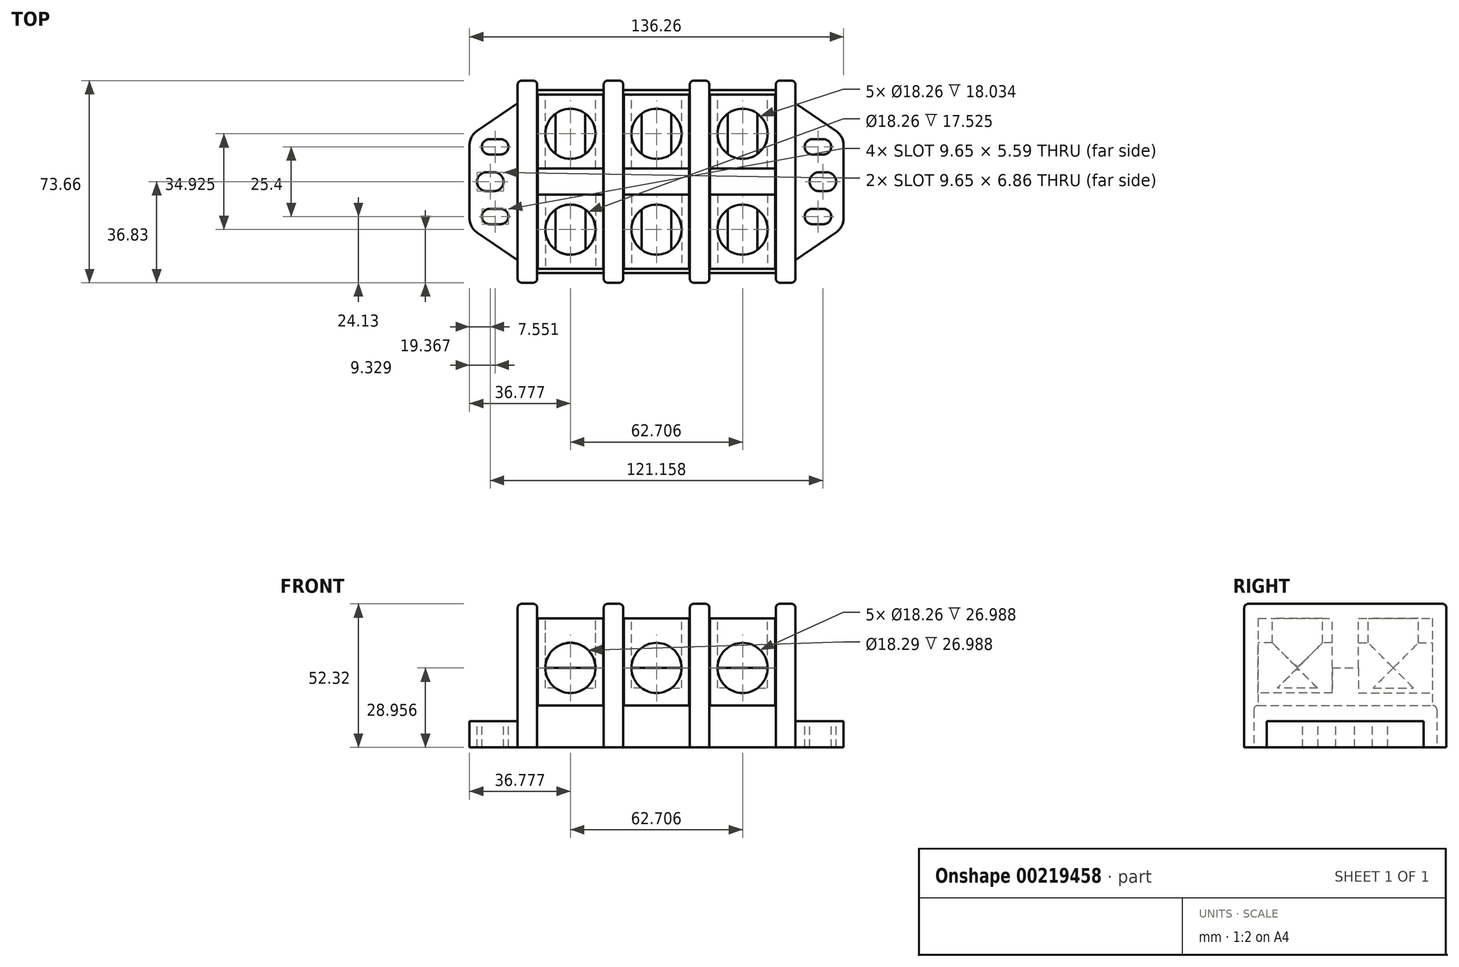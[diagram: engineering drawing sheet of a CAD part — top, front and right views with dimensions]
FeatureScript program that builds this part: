
annotation { "Feature Type Name" : "Feature", "Feature Type Description" : "" }
export const myFeature = defineFeature(function(context is Context, id is Id, definition is map)
    precondition{}
    {
        {
            var Q0;
            Q0=qCreatedBy(makeId("Top.planeOp"),FACE);
            var sketch = newSketch(context, id + "F0", { "sketchPlane" : qUnion([Q0])});
            skPoint(sketch, "E0.middle", {"position": v(0, 0) * mm});
            skLineSegment(sketch, "E1.bottom", {"start": v(-43.46, -36.83) * mm, "end": v(-50.6, -36.83) * mm});
            skLineSegment(sketch, "E1.top", {"start": v(-43.46, 36.83) * mm, "end": v(-50.6, 36.83) * mm});
            skLineSegment(sketch, "E1.left", {"start": v(-43.46, -36.83) * mm, "end": v(-43.46, 36.83) * mm});
            skLineSegment(sketch, "E1.right", {"start": v(-50.6, -36.83) * mm, "end": v(-50.6, 36.83) * mm});
            skPoint(sketch, "E1.middle", {"position": v(-47.03, 0) * mm});
            skLineSegment(sketch, "E2.bottom", {"start": v(43.46, -36.83) * mm, "end": v(50.6, -36.83) * mm});
            skLineSegment(sketch, "E2.top", {"start": v(43.46, 36.83) * mm, "end": v(50.6, 36.83) * mm});
            skLineSegment(sketch, "E2.left", {"start": v(43.46, -36.83) * mm, "end": v(43.46, 36.83) * mm});
            skLineSegment(sketch, "E2.right", {"start": v(50.6, -36.83) * mm, "end": v(50.6, 36.83) * mm});
            skPoint(sketch, "E2.middle", {"position": v(47.03, 0) * mm});
            skLineSegment(sketch, "E3.bottom", {"start": v(-19.25, -36.83) * mm, "end": v(-12.1, -36.83) * mm});
            skLineSegment(sketch, "E3.top", {"start": v(-19.25, 36.83) * mm, "end": v(-12.1, 36.83) * mm});
            skLineSegment(sketch, "E3.left", {"start": v(-19.25, -36.83) * mm, "end": v(-19.25, 36.83) * mm});
            skLineSegment(sketch, "E3.right", {"start": v(-12.1, -36.83) * mm, "end": v(-12.1, 36.83) * mm});
            skPoint(sketch, "E3.middle", {"position": v(-15.68, 0) * mm});
            skLineSegment(sketch, "E4.bottom", {"start": v(19.25, -36.83) * mm, "end": v(12.1, -36.83) * mm});
            skLineSegment(sketch, "E4.top", {"start": v(19.25, 36.83) * mm, "end": v(12.1, 36.83) * mm});
            skLineSegment(sketch, "E4.left", {"start": v(19.25, -36.83) * mm, "end": v(19.25, 36.83) * mm});
            skLineSegment(sketch, "E4.right", {"start": v(12.1, -36.83) * mm, "end": v(12.1, 36.83) * mm});
            skPoint(sketch, "E4.middle", {"position": v(15.68, 0) * mm});
            skSolve(sketch);
        }
        {
            var Q0;
            Q0=qSketchRegion(id+"F0",true);
            extrude(context, id + "F1", {"entities" : qUnion([Q0]), "depth" : 52.32 * mm});
        }
        {
            var Q0;
            Q0=qCreatedBy(makeId("Top.planeOp"),FACE);
            var sketch = newSketch(context, id + "F2", { "sketchPlane" : qUnion([Q0])});
            skLineSegment(sketch, "E5.bottom", {"start": v(-43.46, -33.34) * mm, "end": v(43.46, -33.34) * mm});
            skLineSegment(sketch, "E5.top", {"start": v(-43.46, 33.34) * mm, "end": v(43.46, 33.34) * mm});
            skLineSegment(sketch, "E5.left", {"start": v(-43.46, -33.34) * mm, "end": v(-43.46, 33.34) * mm});
            skLineSegment(sketch, "E5.right", {"start": v(43.46, -33.34) * mm, "end": v(43.46, 33.34) * mm});
            skPoint(sketch, "E5.middle", {"position": v(0, 0) * mm});
            skSolve(sketch);
        }
        {
            var Q0;
            Q0=qSketchRegion(id+"F2",true);
            extrude(context, id + "F3", {"entities" : qUnion([Q0]), "depth" : 15.24 * mm});
        }
        {
            var Q0;
            Q0=qCreatedBy(makeId("Top.planeOp"),FACE);
            var sketch = newSketch(context, id + "F4", { "sketchPlane" : qUnion([Q0])});
            skLineSegment(sketch, "E6", {"start": v(-50.6, 28.58) * mm, "end": v(-68.13, 16.67) * mm});
            skLineSegment(sketch, "E7", {"start": v(-68.13, 16.67) * mm, "end": v(-68.13, -16.67) * mm});
            skLineSegment(sketch, "E8", {"start": v(-68.13, -16.67) * mm, "end": v(-50.6, -28.58) * mm});
            skLineSegment(sketch, "E9", {"start": v(-50.6, -28.58) * mm, "end": v(-50.6, 28.58) * mm});
            skSolve(sketch);
        }
        {
            var Q0;
            Q0=qSketchRegion(id+"F4",true);
            extrude(context, id + "F5", {"entities" : qUnion([Q0]), "operationType" : NewBodyOperationType.ADD, "depth" : 9.52 * mm});
        }
        {
            var Q0;
            Q0=makeQuery(id+"F1.opExtrude","SWEPT_EDGE",EDGE,{"disambiguationData":[OSD([sQuery(id+"F0.wireOp",EDGE,"E1.top"),sQuery(id+"F0.wireOp",EDGE,"E1.right")])]});
            var Q1;
            Q1=makeQuery(id+"F1.opExtrude","CAP_EDGE",EDGE,{"disambiguationData":[OSD([sQuery(id+"F0.wireOp",EDGE,"E1.right")])],"isStart":false});
            var Q2;
            Q2=makeQuery(id+"F1.opExtrude","SWEPT_EDGE",EDGE,{"disambiguationData":[OSD([sQuery(id+"F0.wireOp",EDGE,"E1.bottom"),sQuery(id+"F0.wireOp",EDGE,"E1.right")])]});
            var Q3;
            Q3=makeQuery(id+"F1.opExtrude","SWEPT_EDGE",EDGE,{"disambiguationData":[OSD([sQuery(id+"F0.wireOp",EDGE,"E1.bottom"),sQuery(id+"F0.wireOp",EDGE,"E1.left")])]});
            var Q4;
            Q4=makeQuery(id+"F1.opExtrude","CAP_EDGE",EDGE,{"disambiguationData":[OSD([sQuery(id+"F0.wireOp",EDGE,"E1.left")])],"isStart":false});
            var Q5;
            Q5=makeQuery(id+"F1.opExtrude","CAP_EDGE",EDGE,{"disambiguationData":[OSD([sQuery(id+"F0.wireOp",EDGE,"E1.bottom")])],"isStart":false});
            var Q6;
            Q6=makeQuery(id+"F1.opExtrude","CAP_EDGE",EDGE,{"disambiguationData":[OSD([sQuery(id+"F0.wireOp",EDGE,"E1.top")])],"isStart":false});
            var Q7;
            Q7=makeQuery(id+"F1.opExtrude","SWEPT_EDGE",EDGE,{"disambiguationData":[OSD([sQuery(id+"F0.wireOp",EDGE,"E1.top"),sQuery(id+"F0.wireOp",EDGE,"E1.left")])]});
            var Q8;
            Q8=makeQuery(id+"F3.opExtrude","CAP_EDGE",EDGE,{"disambiguationData":[OSD([sQuery(id+"F2.wireOp",EDGE,"E5.top")])],"isStart":false});
            var Q9;
            Q9=makeQuery(id+"F3.opExtrude","CAP_EDGE",EDGE,{"disambiguationData":[OSD([sQuery(id+"F2.wireOp",EDGE,"E5.bottom")])],"isStart":false});
            var Q10;
            Q10=makeQuery(id+"F1.opExtrude","SWEPT_EDGE",EDGE,{"disambiguationData":[OSD([sQuery(id+"F0.wireOp",EDGE,"E0.bottom"),sQuery(id+"F0.wireOp",EDGE,"E0.left")])]});
            var Q11;
            Q11=makeQuery(id+"F1.opExtrude","CAP_EDGE",EDGE,{"disambiguationData":[OSD([sQuery(id+"F0.wireOp",EDGE,"E0.left")])],"isStart":false});
            var Q12;
            Q12=makeQuery(id+"F1.opExtrude","CAP_EDGE",EDGE,{"disambiguationData":[OSD([sQuery(id+"F0.wireOp",EDGE,"E0.bottom")])],"isStart":false});
            var Q13;
            Q13=makeQuery(id+"F1.opExtrude","SWEPT_EDGE",EDGE,{"disambiguationData":[OSD([sQuery(id+"F0.wireOp",EDGE,"E0.bottom"),sQuery(id+"F0.wireOp",EDGE,"E0.right")])]});
            var Q14;
            Q14=makeQuery(id+"F1.opExtrude","CAP_EDGE",EDGE,{"disambiguationData":[OSD([sQuery(id+"F0.wireOp",EDGE,"E0.right")])],"isStart":false});
            var Q15;
            Q15=makeQuery(id+"F1.opExtrude","CAP_EDGE",EDGE,{"disambiguationData":[OSD([sQuery(id+"F0.wireOp",EDGE,"E0.top")])],"isStart":false});
            var Q16;
            Q16=makeQuery(id+"F1.opExtrude","SWEPT_EDGE",EDGE,{"disambiguationData":[OSD([sQuery(id+"F0.wireOp",EDGE,"E0.top"),sQuery(id+"F0.wireOp",EDGE,"E0.right")])]});
            var Q17;
            Q17=makeQuery(id+"F1.opExtrude","SWEPT_EDGE",EDGE,{"disambiguationData":[OSD([sQuery(id+"F0.wireOp",EDGE,"E0.top"),sQuery(id+"F0.wireOp",EDGE,"E0.left")])]});
            var Q18;
            Q18=makeQuery(id+"F1.opExtrude","SWEPT_EDGE",EDGE,{"disambiguationData":[OSD([sQuery(id+"F0.wireOp",EDGE,"E2.bottom"),sQuery(id+"F0.wireOp",EDGE,"E2.left")])]});
            var Q19;
            Q19=makeQuery(id+"F1.opExtrude","SWEPT_EDGE",EDGE,{"disambiguationData":[OSD([sQuery(id+"F0.wireOp",EDGE,"E2.bottom"),sQuery(id+"F0.wireOp",EDGE,"E2.right")])]});
            var Q20;
            Q20=makeQuery(id+"F1.opExtrude","CAP_EDGE",EDGE,{"disambiguationData":[OSD([sQuery(id+"F0.wireOp",EDGE,"E2.bottom")])],"isStart":false});
            var Q21;
            Q21=makeQuery(id+"F1.opExtrude","CAP_EDGE",EDGE,{"disambiguationData":[OSD([sQuery(id+"F0.wireOp",EDGE,"E2.left")])],"isStart":false});
            var Q22;
            Q22=makeQuery(id+"F1.opExtrude","CAP_EDGE",EDGE,{"disambiguationData":[OSD([sQuery(id+"F0.wireOp",EDGE,"E2.right")])],"isStart":false});
            var Q23;
            Q23=makeQuery(id+"F1.opExtrude","CAP_EDGE",EDGE,{"disambiguationData":[OSD([sQuery(id+"F0.wireOp",EDGE,"E2.top")])],"isStart":false});
            var Q24;
            Q24=makeQuery(id+"F1.opExtrude","SWEPT_EDGE",EDGE,{"disambiguationData":[OSD([sQuery(id+"F0.wireOp",EDGE,"E2.top"),sQuery(id+"F0.wireOp",EDGE,"E2.left")])]});
            var Q25;
            Q25=makeQuery(id+"F1.opExtrude","SWEPT_EDGE",EDGE,{"disambiguationData":[OSD([sQuery(id+"F0.wireOp",EDGE,"E2.top"),sQuery(id+"F0.wireOp",EDGE,"E2.right")])]});
            var Q26;
            Q26=makeQuery(id+"F1.opExtrude","SWEPT_EDGE",EDGE,{"disambiguationData":[OSD([sQuery(id+"F0.wireOp",EDGE,"E3.top"),sQuery(id+"F0.wireOp",EDGE,"E3.left")])]});
            var Q27;
            Q27=makeQuery(id+"F1.opExtrude","CAP_EDGE",EDGE,{"disambiguationData":[OSD([sQuery(id+"F0.wireOp",EDGE,"E3.left")])],"isStart":false});
            var Q28;
            Q28=makeQuery(id+"F1.opExtrude","SWEPT_EDGE",EDGE,{"disambiguationData":[OSD([sQuery(id+"F0.wireOp",EDGE,"E3.bottom"),sQuery(id+"F0.wireOp",EDGE,"E3.left")])]});
            var Q29;
            Q29=makeQuery(id+"F1.opExtrude","SWEPT_EDGE",EDGE,{"disambiguationData":[OSD([sQuery(id+"F0.wireOp",EDGE,"E3.bottom"),sQuery(id+"F0.wireOp",EDGE,"E3.right")])]});
            var Q30;
            Q30=makeQuery(id+"F1.opExtrude","CAP_FACE",FACE,{"disambiguationData":[OSD([sQuery(id+"F0.wireOp",EDGE,"E3.bottom"),sQuery(id+"F0.wireOp",EDGE,"E3.top"),sQuery(id+"F0.wireOp",EDGE,"E3.left"),sQuery(id+"F0.wireOp",EDGE,"E3.right")])],"isStart":false});
            var Q31;
            Q31=makeQuery(id+"F1.opExtrude","SWEPT_EDGE",EDGE,{"disambiguationData":[OSD([sQuery(id+"F0.wireOp",EDGE,"E4.top"),sQuery(id+"F0.wireOp",EDGE,"E4.right")])]});
            var Q32;
            Q32=makeQuery(id+"F1.opExtrude","CAP_EDGE",EDGE,{"disambiguationData":[OSD([sQuery(id+"F0.wireOp",EDGE,"E4.right")])],"isStart":false});
            var Q33;
            Q33=makeQuery(id+"F1.opExtrude","SWEPT_EDGE",EDGE,{"disambiguationData":[OSD([sQuery(id+"F0.wireOp",EDGE,"E4.bottom"),sQuery(id+"F0.wireOp",EDGE,"E4.right")])]});
            var Q34;
            Q34=makeQuery(id+"F1.opExtrude","SWEPT_EDGE",EDGE,{"disambiguationData":[OSD([sQuery(id+"F0.wireOp",EDGE,"E4.bottom"),sQuery(id+"F0.wireOp",EDGE,"E4.left")])]});
            var Q35;
            Q35=makeQuery(id+"F1.opExtrude","CAP_EDGE",EDGE,{"disambiguationData":[OSD([sQuery(id+"F0.wireOp",EDGE,"E4.left")])],"isStart":false});
            var Q36;
            Q36=makeQuery(id+"F1.opExtrude","SWEPT_EDGE",EDGE,{"disambiguationData":[OSD([sQuery(id+"F0.wireOp",EDGE,"E4.top"),sQuery(id+"F0.wireOp",EDGE,"E4.left")])]});
            var Q37;
            Q37=makeQuery(id+"F1.opExtrude","CAP_EDGE",EDGE,{"disambiguationData":[OSD([sQuery(id+"F0.wireOp",EDGE,"E4.bottom")])],"isStart":false});
            var Q38;
            Q38=makeQuery(id+"F1.opExtrude","CAP_EDGE",EDGE,{"disambiguationData":[OSD([sQuery(id+"F0.wireOp",EDGE,"E4.top")])],"isStart":false});
            var Q39;
            Q39=makeQuery(id+"F1.opExtrude","SWEPT_EDGE",EDGE,{"disambiguationData":[OSD([sQuery(id+"F0.wireOp",EDGE,"E3.top"),sQuery(id+"F0.wireOp",EDGE,"E3.right")])]});
            fillet(context, id + "F6", {"entities" : qUnion([Q0, Q1, Q2, Q3, Q4, Q5, Q6, Q7, Q8, Q9, Q10, Q11, Q12, Q13, Q14, Q15, Q16, Q17, Q18, Q19, Q20, Q21, Q22, Q23, Q24, Q25, Q26, Q27, Q28, Q29, Q30, Q31, Q32, Q33, Q34, Q35, Q36, Q37, Q38, Q39]), "radius" : 1.52 * mm, "tangentPropagation" : true});
        }
        {
            var Q0;
            Q0=qCreatedBy(makeId("Top.planeOp"),FACE);
            var sketch = newSketch(context, id + "F7", { "sketchPlane" : qUnion([Q0])});
            skLineSegment(sketch, "E10", {"start": v(50.6, 28.57) * mm, "end": v(68.13, 16.67) * mm});
            skLineSegment(sketch, "E11", {"start": v(68.13, 16.67) * mm, "end": v(68.13, -16.67) * mm});
            skLineSegment(sketch, "E12", {"start": v(68.13, -16.67) * mm, "end": v(50.6, -28.58) * mm});
            skLineSegment(sketch, "E13", {"start": v(50.6, -28.58) * mm, "end": v(50.6, 28.57) * mm});
            skSolve(sketch);
        }
        {
            var Q0;
            Q0=qSketchRegion(id+"F7",true);
            extrude(context, id + "F8", {"entities" : qUnion([Q0]), "operationType" : NewBodyOperationType.ADD, "depth" : 9.52 * mm});
        }
        {
            var Q0;
            Q0=makeQuery(id+"F5.opExtrude","CAP_FACE",FACE,{"disambiguationData":[OSD([sQuery(id+"F4.wireOp",EDGE,"E6"),sQuery(id+"F4.wireOp",EDGE,"E7"),sQuery(id+"F4.wireOp",EDGE,"E8"),sQuery(id+"F4.wireOp",EDGE,"E9")])],"isStart":false});
            var sketch = newSketch(context, id + "F9", { "sketchPlane" : qUnion([Q0])});
            skLineSegment(sketch, "E14.bottom", {"start": v(-56.77, 9.9) * mm, "end": v(-60.83, 9.9) * mm});
            skLineSegment(sketch, "E14.top", {"start": v(-56.77, 15.5) * mm, "end": v(-60.83, 15.5) * mm});
            skLineSegment(sketch, "E14.left", {"start": v(-56.77, 9.9) * mm, "end": v(-56.77, 15.5) * mm});
            skLineSegment(sketch, "E14.right", {"start": v(-60.83, 9.9) * mm, "end": v(-60.83, 15.5) * mm});
            skPoint(sketch, "E14.middle", {"position": v(-58.8, 12.7) * mm});
            skLineSegment(sketch, "E15.bottom", {"start": v(-59.18, -3.43) * mm, "end": v(-61.98, -3.43) * mm});
            skLineSegment(sketch, "E15.top", {"start": v(-59.18, 3.43) * mm, "end": v(-61.98, 3.43) * mm});
            skLineSegment(sketch, "E15.left", {"start": v(-59.18, -3.43) * mm, "end": v(-59.18, 3.43) * mm});
            skLineSegment(sketch, "E15.right", {"start": v(-61.98, -3.43) * mm, "end": v(-61.98, 3.43) * mm});
            skPoint(sketch, "E15.middle", {"position": v(-60.58, 0) * mm});
            skLineSegment(sketch, "E16.bottom", {"start": v(-56.77, -15.5) * mm, "end": v(-60.83, -15.5) * mm});
            skLineSegment(sketch, "E16.top", {"start": v(-56.77, -9.9) * mm, "end": v(-60.83, -9.9) * mm});
            skLineSegment(sketch, "E16.left", {"start": v(-56.77, -15.5) * mm, "end": v(-56.77, -9.9) * mm});
            skLineSegment(sketch, "E16.right", {"start": v(-60.83, -15.5) * mm, "end": v(-60.83, -9.9) * mm});
            skPoint(sketch, "E16.middle", {"position": v(-58.8, -12.7) * mm});
            skPoint(sketch, "E16.middle.positionSnap0", {"position": v(-58.8, 9.9) * mm});
            skPoint(sketch, "E16.centerSnap0", {"position": v(-58.8, 9.9) * mm});
            skArc(sketch, "E17", {"start": v(-60.83, 15.5) * mm, "mid": v(-63.63, 12.7) * mm, "end": v(-60.83, 9.9) * mm});
            skArc(sketch, "E18", {"start": v(-56.77, 9.9) * mm, "mid": v(-53.98, 12.7) * mm, "end": v(-56.77, 15.5) * mm});
            skArc(sketch, "E19", {"start": v(-61.98, 3.43) * mm, "mid": v(-65.4, 0) * mm, "end": v(-61.98, -3.43) * mm});
            skArc(sketch, "E20", {"start": v(-59.18, -3.43) * mm, "mid": v(-55.75, 0) * mm, "end": v(-59.18, 3.43) * mm});
            skArc(sketch, "E21", {"start": v(-60.83, -9.9) * mm, "mid": v(-63.63, -12.7) * mm, "end": v(-60.83, -15.5) * mm});
            skArc(sketch, "E22", {"start": v(-56.77, -15.5) * mm, "mid": v(-53.98, -12.7) * mm, "end": v(-56.77, -9.9) * mm});
            skSolve(sketch);
        }
        {
            var Q0;
            Q0=qSketchRegion(id+"F9",true);
            extrude(context, id + "F10", {"entities" : qUnion([Q0]), "operationType" : NewBodyOperationType.REMOVE, "oppositeDirection" : true, "depth" : 9.52 * mm});
        }
        {
            var Q0;
            Q0=makeQuery(id+"F8.opExtrude","CAP_FACE",FACE,{"disambiguationData":[OSD([sQuery(id+"F7.wireOp",EDGE,"E10"),sQuery(id+"F7.wireOp",EDGE,"E11"),sQuery(id+"F7.wireOp",EDGE,"E12"),sQuery(id+"F7.wireOp",EDGE,"E13")])],"isStart":false});
            var sketch = newSketch(context, id + "F11", { "sketchPlane" : qUnion([Q0])});
            skLineSegment(sketch, "E23.bottom", {"start": v(59.18, -3.43) * mm, "end": v(61.98, -3.43) * mm});
            skLineSegment(sketch, "E23.top", {"start": v(59.18, 3.43) * mm, "end": v(61.98, 3.43) * mm});
            skLineSegment(sketch, "E23.left", {"start": v(59.18, -3.43) * mm, "end": v(59.18, 3.43) * mm});
            skLineSegment(sketch, "E23.right", {"start": v(61.98, -3.43) * mm, "end": v(61.98, 3.43) * mm});
            skPoint(sketch, "E23.middle", {"position": v(60.58, 0) * mm});
            skLineSegment(sketch, "E24.bottom", {"start": v(60.83, 9.9) * mm, "end": v(56.77, 9.9) * mm});
            skLineSegment(sketch, "E24.top", {"start": v(60.83, 15.5) * mm, "end": v(56.77, 15.5) * mm});
            skLineSegment(sketch, "E24.left", {"start": v(60.83, 9.9) * mm, "end": v(60.83, 15.5) * mm});
            skLineSegment(sketch, "E24.right", {"start": v(56.77, 9.9) * mm, "end": v(56.77, 15.5) * mm});
            skPoint(sketch, "E24.middle", {"position": v(58.8, 12.7) * mm});
            skLineSegment(sketch, "E25.bottom", {"start": v(60.83, -15.5) * mm, "end": v(56.77, -15.5) * mm});
            skLineSegment(sketch, "E25.top", {"start": v(60.83, -9.9) * mm, "end": v(56.77, -9.9) * mm});
            skLineSegment(sketch, "E25.left", {"start": v(60.83, -15.5) * mm, "end": v(60.83, -9.9) * mm});
            skLineSegment(sketch, "E25.right", {"start": v(56.77, -15.5) * mm, "end": v(56.77, -9.9) * mm});
            skPoint(sketch, "E25.middle", {"position": v(58.8, -12.7) * mm});
            skArc(sketch, "E26", {"start": v(56.77, 15.5) * mm, "mid": v(53.98, 12.7) * mm, "end": v(56.77, 9.9) * mm});
            skArc(sketch, "E27", {"start": v(60.83, 9.9) * mm, "mid": v(63.63, 12.7) * mm, "end": v(60.83, 15.5) * mm});
            skArc(sketch, "E28", {"start": v(59.18, 3.43) * mm, "mid": v(55.75, 0) * mm, "end": v(59.18, -3.43) * mm});
            skArc(sketch, "E29", {"start": v(61.98, -3.43) * mm, "mid": v(65.4, 0) * mm, "end": v(61.98, 3.43) * mm});
            skArc(sketch, "E30", {"start": v(56.77, -9.9) * mm, "mid": v(53.98, -12.7) * mm, "end": v(56.77, -15.5) * mm});
            skArc(sketch, "E31", {"start": v(60.83, -15.5) * mm, "mid": v(63.63, -12.7) * mm, "end": v(60.83, -9.9) * mm});
            skSolve(sketch);
        }
        {
            var Q0;
            Q0=qSketchRegion(id+"F11",true);
            extrude(context, id + "F12", {"entities" : qUnion([Q0]), "operationType" : NewBodyOperationType.REMOVE, "oppositeDirection" : true, "depth" : 9.52 * mm});
        }
        {
            var Q0;
            Q0=makeQuery(id+"F5.opExtrude","SWEPT_EDGE",EDGE,{"disambiguationData":[OSD([sQuery(id+"F4.wireOp",EDGE,"E6"),sQuery(id+"F4.wireOp",EDGE,"E7")])]});
            var Q1;
            Q1=makeQuery(id+"F5.opExtrude","SWEPT_EDGE",EDGE,{"disambiguationData":[OSD([sQuery(id+"F4.wireOp",EDGE,"E7"),sQuery(id+"F4.wireOp",EDGE,"E8")])]});
            var Q2;
            Q2=makeQuery(id+"F8.opExtrude","SWEPT_EDGE",EDGE,{"disambiguationData":[OSD([sQuery(id+"F7.wireOp",EDGE,"E10"),sQuery(id+"F7.wireOp",EDGE,"E11")])]});
            var Q3;
            Q3=makeQuery(id+"F8.opExtrude","SWEPT_EDGE",EDGE,{"disambiguationData":[OSD([sQuery(id+"F7.wireOp",EDGE,"E11"),sQuery(id+"F7.wireOp",EDGE,"E12")])]});
            fillet(context, id + "F13", {"entities" : qUnion([Q0, Q1, Q2, Q3]), "radius" : 6.35 * mm, "tangentPropagation" : true});
        }
        {
            var Q0;
            Q0=makeQuery(id+"F1.opExtrude","SWEPT_BODY",BODY,{"disambiguationData":[OSD([sQuery(id+"F0.wireOp",EDGE,"E1.bottom"),sQuery(id+"F0.wireOp",EDGE,"E1.top"),sQuery(id+"F0.wireOp",EDGE,"E1.left"),sQuery(id+"F0.wireOp",EDGE,"E1.right")])]});
            var Q1;
            Q1=makeQuery(id+"F1.opExtrude","SWEPT_BODY",BODY,{"disambiguationData":[OSD([sQuery(id+"F0.wireOp",EDGE,"E2.bottom"),sQuery(id+"F0.wireOp",EDGE,"E2.top"),sQuery(id+"F0.wireOp",EDGE,"E2.left"),sQuery(id+"F0.wireOp",EDGE,"E2.right")])]});
            var Q2;
            Q2=makeQuery(id+"F1.opExtrude","SWEPT_BODY",BODY,{"disambiguationData":[OSD([sQuery(id+"F0.wireOp",EDGE,"E3.bottom"),sQuery(id+"F0.wireOp",EDGE,"E3.top"),sQuery(id+"F0.wireOp",EDGE,"E3.left"),sQuery(id+"F0.wireOp",EDGE,"E3.right")])]});
            var Q3;
            Q3=makeQuery(id+"F1.opExtrude","SWEPT_BODY",BODY,{"disambiguationData":[OSD([sQuery(id+"F0.wireOp",EDGE,"E4.bottom"),sQuery(id+"F0.wireOp",EDGE,"E4.top"),sQuery(id+"F0.wireOp",EDGE,"E4.left"),sQuery(id+"F0.wireOp",EDGE,"E4.right")])]});
            var Q4;
            Q4=makeQuery(id+"F3.opExtrude","SWEPT_BODY",BODY,{"disambiguationData":[OSD([sQuery(id+"F2.wireOp",EDGE,"E5.bottom"),sQuery(id+"F2.wireOp",EDGE,"E5.top"),sQuery(id+"F2.wireOp",EDGE,"E5.left"),sQuery(id+"F2.wireOp",EDGE,"E5.right")])]});
            booleanBodies(context, id + "F14", {"operationType" : BooleanOperationType.UNION, "tools" : qUnion([Q0, Q1, Q2, Q3, Q4])});
        }
        {
            var Q0;
            {var subQ0=sQuery(id+"F2.wireOp",EDGE,"E5.top");var subQ1=sQuery(id+"F2.wireOp",EDGE,"E5.bottom");Q0=makeQuery(id+"F14.opBoolean","SPLIT",FACE,{"disambiguationData":[TD([makeQuery(id+"F1.opExtrude","SWEPT_FACE",FACE,{"disambiguationData":[OSD([sQuery(id+"F0.wireOp",EDGE,"E1.left")])]})])],"derivedFrom":makeQuery(id+"F3.opExtrude","CAP_FACE",FACE,{"disambiguationData":[OSD([subQ1,subQ0,sQuery(id+"F2.wireOp",EDGE,"E5.left"),sQuery(id+"F2.wireOp",EDGE,"E5.right")])],"isStart":false})});}
            var sketch = newSketch(context, id + "F15", { "sketchPlane" : qUnion([Q0])});
            skLineSegment(sketch, "E32.bottom", {"start": v(-43.26, -31.75) * mm, "end": v(-19.45, -31.75) * mm});
            skLineSegment(sketch, "E32.top", {"start": v(-43.26, 31.75) * mm, "end": v(-19.45, 31.75) * mm});
            skLineSegment(sketch, "E32.left", {"start": v(-43.26, -31.75) * mm, "end": v(-43.26, 31.75) * mm});
            skLineSegment(sketch, "E32.right", {"start": v(-19.45, -31.75) * mm, "end": v(-19.45, 31.75) * mm});
            skPoint(sketch, "E32.middle", {"position": v(-31.35, 0) * mm});
            skSolve(sketch);
        }
        {
            var Q0;
            {var subQ0=sQuery(id+"F2.wireOp",EDGE,"E5.bottom");var subQ1=sQuery(id+"F2.wireOp",EDGE,"E5.top");Q0=makeQuery(id+"F14.opBoolean","SPLIT",FACE,{"disambiguationData":[TD([makeQuery(id+"F1.opExtrude","SWEPT_FACE",FACE,{"disambiguationData":[OSD([sQuery(id+"F0.wireOp",EDGE,"E3.right")])]})])],"derivedFrom":makeQuery(id+"F3.opExtrude","CAP_FACE",FACE,{"disambiguationData":[OSD([subQ0,subQ1,sQuery(id+"F2.wireOp",EDGE,"E5.left"),sQuery(id+"F2.wireOp",EDGE,"E5.right")])],"isStart":false})});}
            var sketch = newSketch(context, id + "F16", { "sketchPlane" : qUnion([Q0])});
            skLineSegment(sketch, "E33.bottom", {"start": v(-11.9, -31.75) * mm, "end": v(11.9, -31.75) * mm});
            skLineSegment(sketch, "E33.top", {"start": v(-11.9, 31.75) * mm, "end": v(11.9, 31.75) * mm});
            skLineSegment(sketch, "E33.left", {"start": v(-11.9, -31.75) * mm, "end": v(-11.9, 31.75) * mm});
            skLineSegment(sketch, "E33.right", {"start": v(11.9, -31.75) * mm, "end": v(11.9, 31.75) * mm});
            skPoint(sketch, "E33.middle", {"position": v(0, 0) * mm});
            skSolve(sketch);
        }
        {
            var Q0;
            {var subQ0=sQuery(id+"F2.wireOp",EDGE,"E5.bottom");var subQ1=sQuery(id+"F2.wireOp",EDGE,"E5.top");Q0=makeQuery(id+"F14.opBoolean","SPLIT",FACE,{"disambiguationData":[TD([makeQuery(id+"F1.opExtrude","SWEPT_FACE",FACE,{"disambiguationData":[OSD([sQuery(id+"F0.wireOp",EDGE,"E2.left")])]})])],"derivedFrom":makeQuery(id+"F3.opExtrude","CAP_FACE",FACE,{"disambiguationData":[OSD([subQ0,subQ1,sQuery(id+"F2.wireOp",EDGE,"E5.left"),sQuery(id+"F2.wireOp",EDGE,"E5.right")])],"isStart":false})});}
            var sketch = newSketch(context, id + "F17", { "sketchPlane" : qUnion([Q0])});
            skLineSegment(sketch, "E34.bottom", {"start": v(19.45, -31.75) * mm, "end": v(43.26, -31.75) * mm});
            skLineSegment(sketch, "E34.top", {"start": v(19.45, 31.75) * mm, "end": v(43.26, 31.75) * mm});
            skLineSegment(sketch, "E34.left", {"start": v(19.45, -31.75) * mm, "end": v(19.45, 31.75) * mm});
            skLineSegment(sketch, "E34.right", {"start": v(43.26, -31.75) * mm, "end": v(43.26, 31.75) * mm});
            skPoint(sketch, "E34.middle", {"position": v(31.35, 0) * mm});
            skPoint(sketch, "E34.middle.positionSnap0", {"position": v(19.25, 0) * mm});
            skPoint(sketch, "E34.centerSnap0", {"position": v(19.25, 0) * mm});
            skSolve(sketch);
        }
        {
            var Q0;
            Q0=qSketchRegion(id+"F15",true);
            var Q1;
            Q1=qSketchRegion(id+"F16",true);
            var Q2;
            Q2=qSketchRegion(id+"F17",true);
            extrude(context, id + "F18", {"entities" : qUnion([Q0, Q1, Q2]), "depth" : 31.75 * mm});
        }
        {
            var Q0;
            Q0=makeQuery(id+"F18.opExtrude","CAP_FACE",FACE,{"disambiguationData":[OSD([sQuery(id+"F15.wireOp",EDGE,"E32.bottom"),sQuery(id+"F15.wireOp",EDGE,"E32.top"),sQuery(id+"F15.wireOp",EDGE,"E32.left"),sQuery(id+"F15.wireOp",EDGE,"E32.right")])],"isStart":false});
            var sketch = newSketch(context, id + "F19", { "sketchPlane" : qUnion([Q0])});
            skCircle(sketch, "E35", {"center": v(-31.35, 17.46) * mm, "radius": 9.13 * mm});
            skPoint(sketch, "E35.centerSnap0", {"position": v(-31.35, 31.75) * mm});
            skCircle(sketch, "E36", {"center": v(-31.35, -17.46) * mm, "radius": 9.13 * mm});
            skSolve(sketch);
        }
        {
            var Q0;
            Q0=qSketchRegion(id+"F19",true);
            extrude(context, id + "F20", {"entities" : qUnion([Q0]), "operationType" : NewBodyOperationType.REMOVE, "oppositeDirection" : true, "depth" : 25.4 * mm});
        }
        {
            var Q0;
            Q0=makeQuery(id+"F18.opExtrude","CAP_FACE",FACE,{"disambiguationData":[OSD([sQuery(id+"F16.wireOp",EDGE,"E33.bottom"),sQuery(id+"F16.wireOp",EDGE,"E33.top"),sQuery(id+"F16.wireOp",EDGE,"E33.left"),sQuery(id+"F16.wireOp",EDGE,"E33.right")])],"isStart":false});
            var sketch = newSketch(context, id + "F21", { "sketchPlane" : qUnion([Q0])});
            skCircle(sketch, "E37", {"center": v(0, 17.46) * mm, "radius": 9.13 * mm});
            skPoint(sketch, "E37.centerSnap0", {"position": v(0, 31.75) * mm});
            skCircle(sketch, "E38", {"center": v(0, -17.46) * mm, "radius": 9.13 * mm});
            skSolve(sketch);
        }
        {
            var Q0;
            Q0=qSketchRegion(id+"F21",true);
            extrude(context, id + "F22", {"entities" : qUnion([Q0]), "operationType" : NewBodyOperationType.REMOVE, "oppositeDirection" : true, "depth" : 25.4 * mm});
        }
        {
            var Q0;
            Q0=makeQuery(id+"F18.opExtrude","CAP_FACE",FACE,{"disambiguationData":[OSD([sQuery(id+"F17.wireOp",EDGE,"E34.bottom"),sQuery(id+"F17.wireOp",EDGE,"E34.top"),sQuery(id+"F17.wireOp",EDGE,"E34.left"),sQuery(id+"F17.wireOp",EDGE,"E34.right")])],"isStart":false});
            var sketch = newSketch(context, id + "F23", { "sketchPlane" : qUnion([Q0])});
            skCircle(sketch, "E39", {"center": v(31.35, 17.46) * mm, "radius": 9.13 * mm});
            skPoint(sketch, "E39.centerSnap0", {"position": v(31.35, 31.75) * mm});
            skCircle(sketch, "E40", {"center": v(31.35, -17.46) * mm, "radius": 9.13 * mm});
            skSolve(sketch);
        }
        {
            var Q0;
            Q0=qSketchRegion(id+"F23",true);
            extrude(context, id + "F24", {"entities" : qUnion([Q0]), "operationType" : NewBodyOperationType.REMOVE, "oppositeDirection" : true, "depth" : 25.4 * mm});
        }
        {
            var Q0;
            Q0=makeQuery(id+"F18.opExtrude","CAP_FACE",FACE,{"disambiguationData":[OSD([sQuery(id+"F15.wireOp",EDGE,"E32.bottom"),sQuery(id+"F15.wireOp",EDGE,"E32.top"),sQuery(id+"F15.wireOp",EDGE,"E32.left"),sQuery(id+"F15.wireOp",EDGE,"E32.right")])],"isStart":false});
            var sketch = newSketch(context, id + "F25", { "sketchPlane" : qUnion([Q0])});
            skLineSegment(sketch, "E41.bottom", {"start": v(-43.26, 4.76) * mm, "end": v(-19.45, 4.76) * mm});
            skLineSegment(sketch, "E41.top", {"start": v(-43.26, -4.76) * mm, "end": v(-19.45, -4.76) * mm});
            skLineSegment(sketch, "E41.left", {"start": v(-43.26, 4.76) * mm, "end": v(-43.26, -4.76) * mm});
            skLineSegment(sketch, "E41.right", {"start": v(-19.45, 4.76) * mm, "end": v(-19.45, -4.76) * mm});
            skSolve(sketch);
        }
        {
            var Q0;
            Q0=qSketchRegion(id+"F25",true);
            extrude(context, id + "F26", {"entities" : qUnion([Q0]), "operationType" : NewBodyOperationType.REMOVE, "oppositeDirection" : true, "depth" : 18.03 * mm});
        }
        {
            var Q0;
            Q0=makeQuery(id+"F18.opExtrude","CAP_FACE",FACE,{"disambiguationData":[OSD([sQuery(id+"F16.wireOp",EDGE,"E33.bottom"),sQuery(id+"F16.wireOp",EDGE,"E33.top"),sQuery(id+"F16.wireOp",EDGE,"E33.left"),sQuery(id+"F16.wireOp",EDGE,"E33.right")])],"isStart":false});
            var sketch = newSketch(context, id + "F27", { "sketchPlane" : qUnion([Q0])});
            skLineSegment(sketch, "E42.bottom", {"start": v(-11.9, 4.76) * mm, "end": v(11.9, 4.76) * mm});
            skLineSegment(sketch, "E42.top", {"start": v(-11.9, -4.76) * mm, "end": v(11.9, -4.76) * mm});
            skLineSegment(sketch, "E42.left", {"start": v(-11.9, 4.76) * mm, "end": v(-11.9, -4.76) * mm});
            skLineSegment(sketch, "E42.right", {"start": v(11.9, 4.76) * mm, "end": v(11.9, -4.76) * mm});
            skSolve(sketch);
        }
        {
            var Q0;
            Q0=qSketchRegion(id+"F27",true);
            extrude(context, id + "F28", {"entities" : qUnion([Q0]), "operationType" : NewBodyOperationType.REMOVE, "oppositeDirection" : true, "depth" : 18.03 * mm});
        }
        {
            var Q0;
            Q0=makeQuery(id+"F18.opExtrude","CAP_FACE",FACE,{"disambiguationData":[OSD([sQuery(id+"F17.wireOp",EDGE,"E34.bottom"),sQuery(id+"F17.wireOp",EDGE,"E34.top"),sQuery(id+"F17.wireOp",EDGE,"E34.left"),sQuery(id+"F17.wireOp",EDGE,"E34.right")])],"isStart":false});
            var sketch = newSketch(context, id + "F29", { "sketchPlane" : qUnion([Q0])});
            skLineSegment(sketch, "E43.bottom", {"start": v(19.45, 4.76) * mm, "end": v(43.26, 4.76) * mm});
            skLineSegment(sketch, "E43.top", {"start": v(19.45, -4.76) * mm, "end": v(43.26, -4.76) * mm});
            skLineSegment(sketch, "E43.left", {"start": v(19.45, 4.76) * mm, "end": v(19.45, -4.76) * mm});
            skLineSegment(sketch, "E43.right", {"start": v(43.26, 4.76) * mm, "end": v(43.26, -4.76) * mm});
            skSolve(sketch);
        }
        {
            var Q0;
            Q0=qSketchRegion(id+"F29",true);
            extrude(context, id + "F30", {"entities" : qUnion([Q0]), "operationType" : NewBodyOperationType.REMOVE, "oppositeDirection" : true, "depth" : 18.03 * mm});
        }
        {
            var Q0;
            Q0=makeQuery(id+"F18.opExtrude","SWEPT_FACE",FACE,{"disambiguationData":[OSD([sQuery(id+"F15.wireOp",EDGE,"E32.bottom")])]});
            var sketch = newSketch(context, id + "F31", { "sketchPlane" : qUnion([Q0])});
            skCircle(sketch, "E44", {"center": v(-31.35, 28.96) * mm, "radius": 9.14 * mm});
            skPoint(sketch, "E44.centerSnap0", {"position": v(-31.35, 47) * mm});
            skSolve(sketch);
        }
        {
            var Q0;
            Q0=qSketchRegion(id+"F31",true);
            extrude(context, id + "F32", {"entities" : qUnion([Q0]), "operationType" : NewBodyOperationType.REMOVE, "oppositeDirection" : true, "depth" : 26.99 * mm});
        }
        {
            var Q0;
            Q0=makeQuery(id+"F18.opExtrude","SWEPT_FACE",FACE,{"disambiguationData":[OSD([sQuery(id+"F16.wireOp",EDGE,"E33.bottom")])]});
            var sketch = newSketch(context, id + "F33", { "sketchPlane" : qUnion([Q0])});
            skCircle(sketch, "E45", {"center": v(0, 28.96) * mm, "radius": 9.13 * mm});
            skPoint(sketch, "E45.centerSnap0", {"position": v(0, 47) * mm});
            skSolve(sketch);
        }
        {
            var Q0;
            Q0=qSketchRegion(id+"F33",true);
            extrude(context, id + "F34", {"entities" : qUnion([Q0]), "operationType" : NewBodyOperationType.REMOVE, "oppositeDirection" : true, "depth" : 26.99 * mm});
        }
        {
            var Q0;
            Q0=makeQuery(id+"F18.opExtrude","SWEPT_FACE",FACE,{"disambiguationData":[OSD([sQuery(id+"F17.wireOp",EDGE,"E34.bottom")])]});
            var sketch = newSketch(context, id + "F35", { "sketchPlane" : qUnion([Q0])});
            skCircle(sketch, "E46", {"center": v(31.35, 28.96) * mm, "radius": 9.13 * mm});
            skPoint(sketch, "E46.centerSnap0", {"position": v(31.35, 47) * mm});
            skSolve(sketch);
        }
        {
            var Q0;
            Q0=qSketchRegion(id+"F35",true);
            extrude(context, id + "F36", {"entities" : qUnion([Q0]), "operationType" : NewBodyOperationType.REMOVE, "oppositeDirection" : true, "depth" : 26.99 * mm});
        }
        {
            var Q0;
            Q0=makeQuery(id+"F18.opExtrude","SWEPT_FACE",FACE,{"disambiguationData":[OSD([sQuery(id+"F17.wireOp",EDGE,"E34.top")])]});
            var sketch = newSketch(context, id + "F37", { "sketchPlane" : qUnion([Q0])});
            skCircle(sketch, "E47", {"center": v(-31.35, 28.96) * mm, "radius": 9.13 * mm});
            skPoint(sketch, "E47.centerSnap0", {"position": v(-31.35, 47) * mm});
            skSolve(sketch);
        }
        {
            var Q0;
            Q0=qSketchRegion(id+"F37",true);
            extrude(context, id + "F38", {"entities" : qUnion([Q0]), "operationType" : NewBodyOperationType.REMOVE, "oppositeDirection" : true, "depth" : 26.99 * mm});
        }
        {
            var Q0;
            Q0=makeQuery(id+"F18.opExtrude","SWEPT_FACE",FACE,{"disambiguationData":[OSD([sQuery(id+"F16.wireOp",EDGE,"E33.top")])]});
            var sketch = newSketch(context, id + "F39", { "sketchPlane" : qUnion([Q0])});
            skCircle(sketch, "E48", {"center": v(0, 28.96) * mm, "radius": 9.13 * mm});
            skPoint(sketch, "E48.centerSnap0", {"position": v(0, 47) * mm});
            skSolve(sketch);
        }
        {
            var Q0;
            Q0=qSketchRegion(id+"F39",true);
            extrude(context, id + "F40", {"entities" : qUnion([Q0]), "operationType" : NewBodyOperationType.REMOVE, "oppositeDirection" : true, "depth" : 26.99 * mm});
        }
        {
            var Q0;
            Q0=makeQuery(id+"F18.opExtrude","SWEPT_FACE",FACE,{"disambiguationData":[OSD([sQuery(id+"F15.wireOp",EDGE,"E32.top")])]});
            var sketch = newSketch(context, id + "F41", { "sketchPlane" : qUnion([Q0])});
            skCircle(sketch, "E49", {"center": v(31.35, 28.96) * mm, "radius": 9.13 * mm});
            skPoint(sketch, "E49.centerSnap0", {"position": v(31.35, 47) * mm});
            skSolve(sketch);
        }
        {
            var Q0;
            Q0=qSketchRegion(id+"F41",true);
            extrude(context, id + "F42", {"entities" : qUnion([Q0]), "operationType" : NewBodyOperationType.REMOVE, "oppositeDirection" : true, "depth" : 26.99 * mm});
        }
    });
